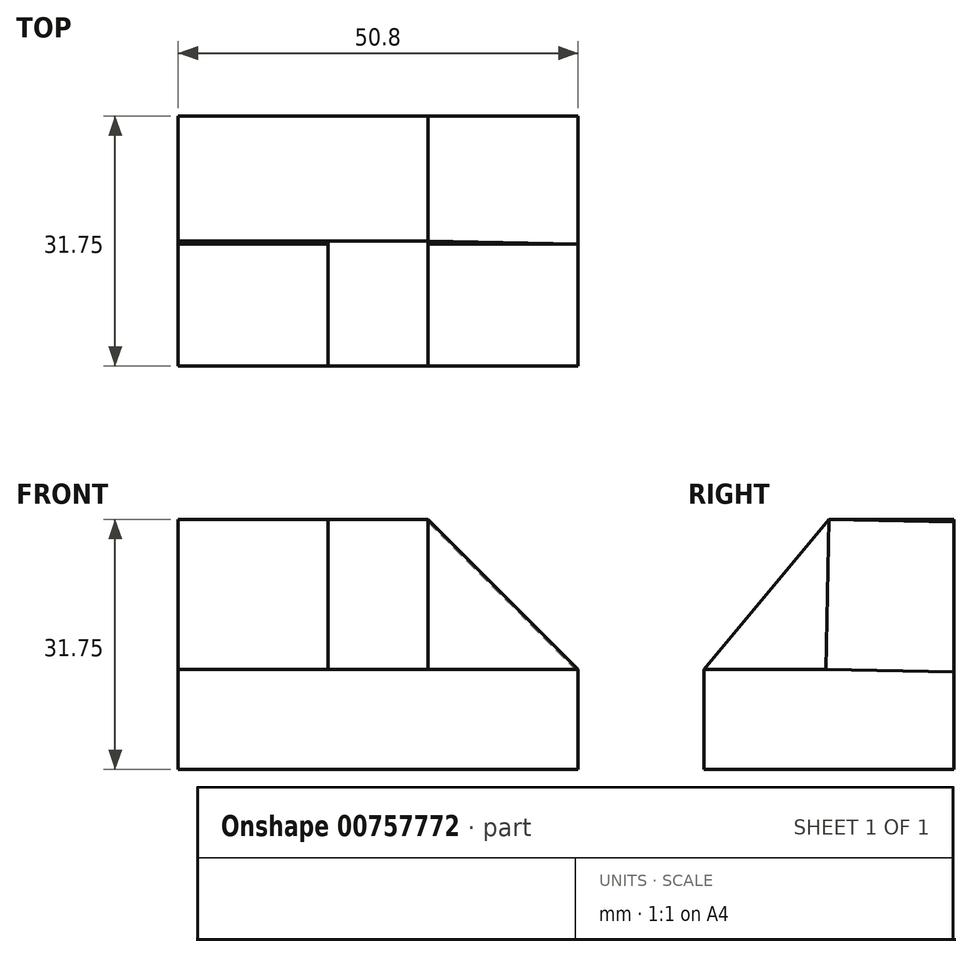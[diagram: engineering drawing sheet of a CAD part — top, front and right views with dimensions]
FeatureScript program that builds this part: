
annotation { "Feature Type Name" : "Feature", "Feature Type Description" : "" }
export const myFeature = defineFeature(function(context is Context, id is Id, definition is map)
    precondition{}
    {
        {
            var Q0;
            Q0=qCreatedBy(makeId("Front.planeOp"),FACE);
            var sketch = newSketch(context, id + "F0", { "sketchPlane" : qUnion([Q0])});
            skLineSegment(sketch, "E0", {"start": v(-24.47, 0) * mm, "end": v(26.33, 0) * mm});
            skLineSegment(sketch, "E1", {"start": v(26.33, 0) * mm, "end": v(26.33, 31.75) * mm});
            skLineSegment(sketch, "E2", {"start": v(26.33, 31.75) * mm, "end": v(-24.47, 31.75) * mm});
            skLineSegment(sketch, "E3", {"start": v(-24.47, 31.75) * mm, "end": v(-24.47, 0) * mm});
            skSolve(sketch);
        }
        {
            var Q0;
            Q0 = qSketchRegion(id + "F0", true);
            extrude(context, id + "F1", {"entities" : qUnion([Q0]), "depth" : 31.75 * mm, "offsetDistance" : 25.4 * mm});
        }
        {
            var Q0;
            Q0=makeQuery(id+"F1.opExtrude","SWEPT_FACE",FACE,{"disambiguationData":[OSD([sQuery(id+"F0.wireOp",EDGE,"E1")])]});
            var sketch = newSketch(context, id + "F2", { "sketchPlane" : qUnion([Q0])});
            skLineSegment(sketch, "E4", {"start": v(-31.75, 12.7) * mm, "end": v(-15.88, 31.75) * mm});
            skSolve(sketch);
        }
        {
            var Q0;
            Q0 = qSketchRegion(id + "F2", true);
            var Q1;
            {var subQ0=sQuery(id+"F2.wireOp",EDGE,"E4");Q1=makeQuery(id+"F2.imprint","IMPRINT",FACE,{"disambiguationData":[TD([[makeQuery(id+"F2.imprint","IMPRINT",EDGE,{"derivedFrom":subQ0}),1.0]])]});}
            extrude(context, id + "F3", {"entities" : qUnion([Q0, Q1]), "operationType" : NewBodyOperationType.REMOVE, "endBound" : BoundingType.THROUGH_ALL, "oppositeDirection" : true, "depth" : 25.4 * mm, "offsetDistance" : 25.4 * mm});
        }
        {
            var Q0;
            Q0=makeQuery(id+"F1.opExtrude","SWEPT_FACE",FACE,{"disambiguationData":[OSD([sQuery(id+"F0.wireOp",EDGE,"E1")])]});
            var sketch = newSketch(context, id + "F4", { "sketchPlane" : qUnion([Q0])});
            skLineSegment(sketch, "E5", {"start": v(-31.75, 12.7) * mm, "end": v(-16.26, 12.7) * mm});
            skLineSegment(sketch, "E6", {"start": v(-16.26, 12.7) * mm, "end": v(-15.88, 31.75) * mm});
            skSolve(sketch);
        }
        {
            var Q0;
            Q0 = qSketchRegion(id + "F4", true);
            var Q1;
            Q1=makeQuery(id+"F4.imprint","IMPRINT",FACE,{"disambiguationData":[TD([[makeQuery(id+"F4.imprint","IMPRINT",EDGE,{"derivedFrom":sQuery(id+"F4.wireOp",EDGE,"E5")}),1.0]])]});
            extrude(context, id + "F5", {"entities" : qUnion([Q0, Q1]), "operationType" : NewBodyOperationType.REMOVE, "oppositeDirection" : true, "depth" : 19.05 * mm, "offsetDistance" : 25.4 * mm});
        }
        {
            var Q0;
            Q0=makeQuery(id+"F1.opExtrude","SWEPT_FACE",FACE,{"disambiguationData":[OSD([sQuery(id+"F0.wireOp",EDGE,"E3")])]});
            var sketch = newSketch(context, id + "F6", { "sketchPlane" : qUnion([Q0])});
            skLineSegment(sketch, "E7", {"start": v(31.75, 12.7) * mm, "end": v(16.26, 12.7) * mm});
            skLineSegment(sketch, "E8", {"start": v(16.26, 12.7) * mm, "end": v(15.87, 31.75) * mm});
            skSolve(sketch);
        }
        {
            var Q0;
            Q0 = qSketchRegion(id + "F6", true);
            var Q1;
            Q1=makeQuery(id+"F6.imprint","IMPRINT",FACE,{"disambiguationData":[TD([[makeQuery(id+"F6.imprint","IMPRINT",EDGE,{"derivedFrom":sQuery(id+"F6.wireOp",EDGE,"E7")}),-1.0]])]});
            extrude(context, id + "F7", {"entities" : qUnion([Q0, Q1]), "operationType" : NewBodyOperationType.REMOVE, "oppositeDirection" : true, "depth" : 19.05 * mm, "offsetDistance" : 25.4 * mm});
        }
        {
            var Q0;
            Q0=makeQuery(id+"F5.boolean.opBoolean","COPY",FACE,{"derivedFrom":makeQuery(id+"F5.opExtrude","SWEPT_FACE",FACE,{"disambiguationData":[OSD([sQuery(id+"F4.wireOp",EDGE,"E6")])]})});
            var sketch = newSketch(context, id + "F8", { "sketchPlane" : qUnion([Q0])});
            skLineSegment(sketch, "E9", {"start": v(26.33, 31.43) * mm, "end": v(7.28, 31.43) * mm});
            skLineSegment(sketch, "E10", {"start": v(7.28, 31.43) * mm, "end": v(26.33, 12.37) * mm});
            skLineSegment(sketch, "E11", {"start": v(26.33, 12.37) * mm, "end": v(26.33, 31.43) * mm});
            skSolve(sketch);
        }
        {
            var Q0;
            Q0 = qSketchRegion(id + "F8", true);
            extrude(context, id + "F9", {"entities" : qUnion([Q0]), "operationType" : NewBodyOperationType.REMOVE, "endBound" : BoundingType.THROUGH_ALL, "oppositeDirection" : true, "depth" : 25.4 * mm, "offsetDistance" : 25.4 * mm});
        }
        {
            var Q0;
            Q0=makeQuery(id+"F1.opExtrude","SWEPT_FACE",FACE,{"disambiguationData":[OSD([sQuery(id+"F0.wireOp",EDGE,"E2")])]});
            var sketch = newSketch(context, id + "F10", { "sketchPlane" : qUnion([Q0])});
            skLineSegment(sketch, "E12", {"start": v(7.28, -15.88) * mm, "end": v(7.28, 0) * mm});
            skSolve(sketch);
        }
        {
            var Q0;
            Q0=makeQuery(id+"F9.boolean.opBoolean","COPY",FACE,{"derivedFrom":makeQuery(id+"F9.opExtrude","SWEPT_FACE",FACE,{"disambiguationData":[OSD([sQuery(id+"F8.wireOp",EDGE,"E9")])]})});
            extrude(context, id + "F11", {"entities" : qUnion([Q0]), "operationType" : NewBodyOperationType.REMOVE, "oppositeDirection" : true, "depth" : 25.4 * mm, "offsetDistance" : 25.4 * mm});
        }
        {
            var Q0;
            {var subQ0=sQuery(id+"F10.wireOp",EDGE,"E12");Q0=makeQuery(id+"F10.imprint","IMPRINT",FACE,{"disambiguationData":[TD([[makeQuery(id+"F10.imprint","IMPRINT",EDGE,{"derivedFrom":subQ0}),-1.0]])]});}
            extrude(context, id + "F12", {"entities" : qUnion([Q0]), "operationType" : NewBodyOperationType.REMOVE, "depth" : 12.95 * mm, "offsetDistance" : 25.4 * mm});
        }
    });
